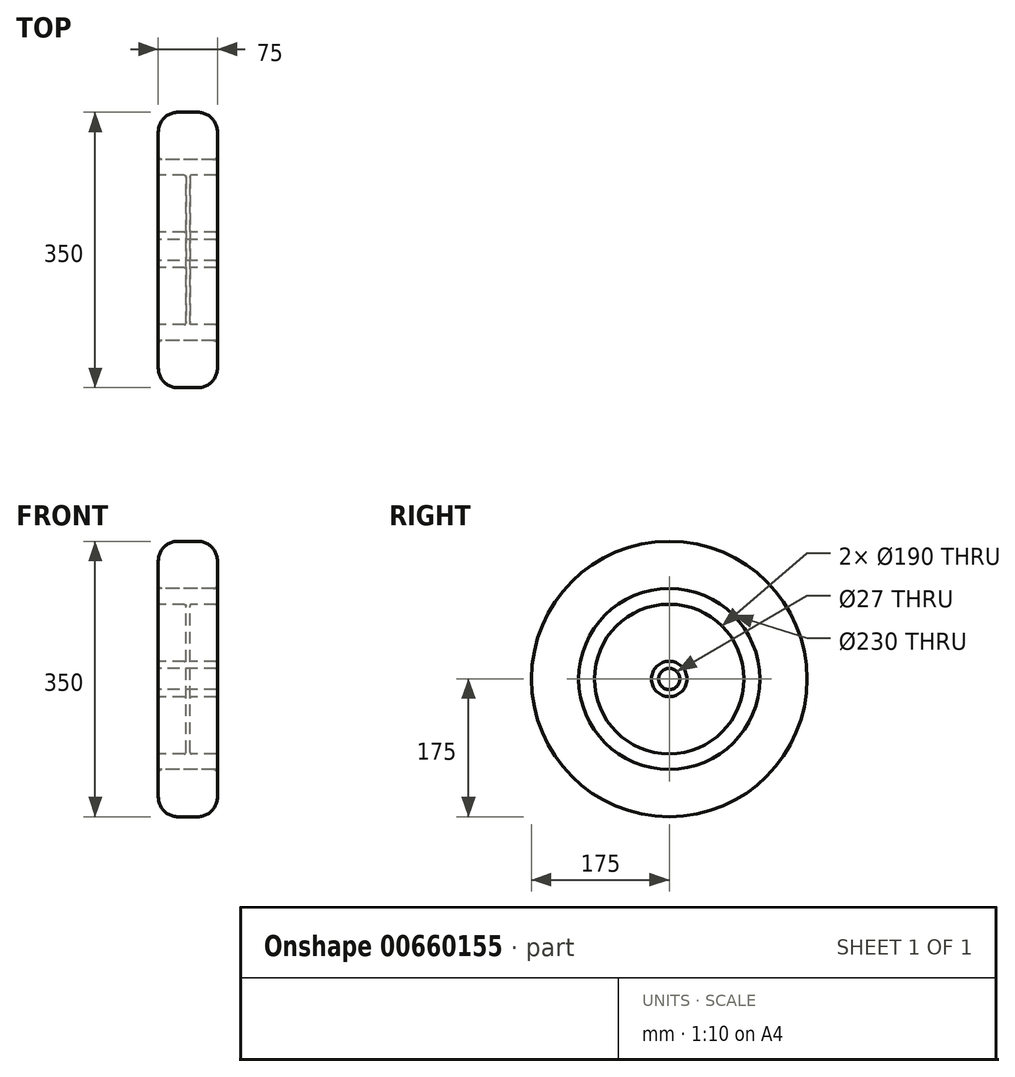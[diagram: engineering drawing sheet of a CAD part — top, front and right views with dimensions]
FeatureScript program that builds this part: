
annotation { "Feature Type Name" : "Feature", "Feature Type Description" : "" }
export const myFeature = defineFeature(function(context is Context, id is Id, definition is map)
    precondition{}
    {
        {
            var Q0;
            Q0=qCreatedBy(makeId("Right.planeOp"),FACE);
            var sketch = newSketch(context, id + "F0", { "sketchPlane" : qUnion([Q0])});
            skCircle(sketch, "E0", {"center": v(0, 0) * mm, "radius": 22.5 * mm});
            skCircle(sketch, "E1", {"center": v(0, 0) * mm, "radius": 115 * mm});
            skCircle(sketch, "E2", {"center": v(0, 0) * mm, "radius": 175 * mm});
            skCircle(sketch, "E3", {"center": v(0, 0) * mm, "radius": 13.5 * mm});
            skCircle(sketch, "E4", {"center": v(0, 0) * mm, "radius": 95 * mm});
            skSolve(sketch);
        }
        {
            var Q0;
            Q0=makeQuery(id+"F0.imprint","IMPRINT",FACE,{"disambiguationData":[TD([[makeQuery(id+"F0.imprint","IMPRINT",EDGE,{"derivedFrom":sQuery(id+"F0.wireOp",EDGE,"E1")}),-1.0]])]});
            extrude(context, id + "F1", {"entities" : qUnion([Q0]), "depth" : 75 * mm, "symmetric" : true});
        }
        {
            var Q0;
            Q0=makeQuery(id+"F0.imprint","IMPRINT",FACE,{"disambiguationData":[TD([[makeQuery(id+"F0.imprint","IMPRINT",EDGE,{"derivedFrom":sQuery(id+"F0.wireOp",EDGE,"E1")}),1.0]])]});
            var Q1;
            Q1=makeQuery(id+"F0.imprint","IMPRINT",FACE,{"disambiguationData":[TD([[makeQuery(id+"F0.imprint","IMPRINT",EDGE,{"derivedFrom":sQuery(id+"F0.wireOp",EDGE,"E0")}),1.0]])]});
            extrude(context, id + "F2", {"entities" : qUnion([Q0, Q1]), "depth" : 75 * mm, "symmetric" : true});
        }
        {
            var Q0;
            Q0=makeQuery(id+"F0.imprint","IMPRINT",FACE,{"disambiguationData":[TD([[makeQuery(id+"F0.imprint","IMPRINT",EDGE,{"derivedFrom":sQuery(id+"F0.wireOp",EDGE,"E0")}),-1.0]])]});
            extrude(context, id + "F3", {"entities" : qUnion([Q0]), "operationType" : NewBodyOperationType.ADD, "depth" : 5 * mm, "symmetric" : true});
        }
        {
            var Q0;
            Q0=makeQuery(id+"F1.opExtrude","CAP_EDGE",EDGE,{"disambiguationData":[OSD([sQuery(id+"F0.wireOp",EDGE,"E2")])],"isStart":false});
            var Q1;
            Q1=makeQuery(id+"F1.opExtrude","CAP_EDGE",EDGE,{"disambiguationData":[OSD([sQuery(id+"F0.wireOp",EDGE,"E2")])],"isStart":true});
            fillet(context, id + "F4", {"entities" : qUnion([Q0, Q1]), "radius" : 25 * mm, "tangentPropagation" : true, "allowEdgeOverflow" : false});
        }
        {
            var Q0;
            {var subQ0=sQuery(id+"F0.wireOp",EDGE,"E0");Q0=makeQuery(id+"F3.boolean.opBoolean","SPLIT",FACE,{"disambiguationData":[TD([makeQuery(id+"F2.opExtrude","CAP_FACE",FACE,{"disambiguationData":[OSD([subQ0,sQuery(id+"F0.wireOp",EDGE,"E3")])],"isStart":false})])],"derivedFrom":makeQuery(id+"F2.opExtrude","SWEPT_FACE",FACE,{"disambiguationData":[OSD([subQ0])]})});}
            var Q1;
            {var subQ0=sQuery(id+"F0.wireOp",EDGE,"E4");Q1=makeQuery(id+"F3.boolean.opBoolean","SPLIT",FACE,{"disambiguationData":[TD([makeQuery(id+"F2.opExtrude","CAP_FACE",FACE,{"disambiguationData":[OSD([sQuery(id+"F0.wireOp",EDGE,"E1"),subQ0])],"isStart":false})])],"derivedFrom":makeQuery(id+"F2.opExtrude","SWEPT_FACE",FACE,{"disambiguationData":[OSD([subQ0])]})});}
            var Q2;
            {var subQ0=sQuery(id+"F0.wireOp",EDGE,"E4");Q2=makeQuery(id+"F3.boolean.opBoolean","SPLIT",FACE,{"disambiguationData":[TD([makeQuery(id+"F2.opExtrude","CAP_FACE",FACE,{"disambiguationData":[OSD([sQuery(id+"F0.wireOp",EDGE,"E1"),subQ0])],"isStart":true})])],"derivedFrom":makeQuery(id+"F2.opExtrude","SWEPT_FACE",FACE,{"disambiguationData":[OSD([subQ0])]})});}
            var Q3;
            {var subQ0=sQuery(id+"F0.wireOp",EDGE,"E0");Q3=makeQuery(id+"F3.boolean.opBoolean","SPLIT",FACE,{"disambiguationData":[TD([makeQuery(id+"F2.opExtrude","CAP_FACE",FACE,{"disambiguationData":[OSD([subQ0,sQuery(id+"F0.wireOp",EDGE,"E3")])],"isStart":true})])],"derivedFrom":makeQuery(id+"F2.opExtrude","SWEPT_FACE",FACE,{"disambiguationData":[OSD([subQ0])]})});}
            var Q4;
            Q4=makeQuery(id+"F2.opExtrude","SWEPT_FACE",FACE,{"disambiguationData":[OSD([sQuery(id+"F0.wireOp",EDGE,"E3")])]});
            fillet(context, id + "F5", {"entities" : qUnion([Q0, Q1, Q2, Q3, Q4]), "radius" : 2 * mm, "tangentPropagation" : true, "allowEdgeOverflow" : false});
        }
        {
            var Q0;
            Q0=makeQuery(id+"F1.opExtrude","CAP_EDGE",EDGE,{"disambiguationData":[OSD([sQuery(id+"F0.wireOp",EDGE,"E1")])],"isStart":true});
            var Q1;
            Q1=makeQuery(id+"F1.opExtrude","CAP_EDGE",EDGE,{"disambiguationData":[OSD([sQuery(id+"F0.wireOp",EDGE,"E1")])],"isStart":false});
            fillet(context, id + "F6", {"entities" : qUnion([Q0, Q1]), "radius" : 5 * mm, "tangentPropagation" : true, "allowEdgeOverflow" : false});
        }
        {
            var Q0;
            Q0=makeQuery(id+"F2.opExtrude","CAP_EDGE",EDGE,{"disambiguationData":[OSD([sQuery(id+"F0.wireOp",EDGE,"E1")])],"isStart":true});
            var Q1;
            Q1=makeQuery(id+"F2.opExtrude","CAP_EDGE",EDGE,{"disambiguationData":[OSD([sQuery(id+"F0.wireOp",EDGE,"E1")])],"isStart":false});
            fillet(context, id + "F7", {"entities" : qUnion([Q0, Q1]), "radius" : 2 * mm, "tangentPropagation" : true, "allowEdgeOverflow" : false});
        }
    });
